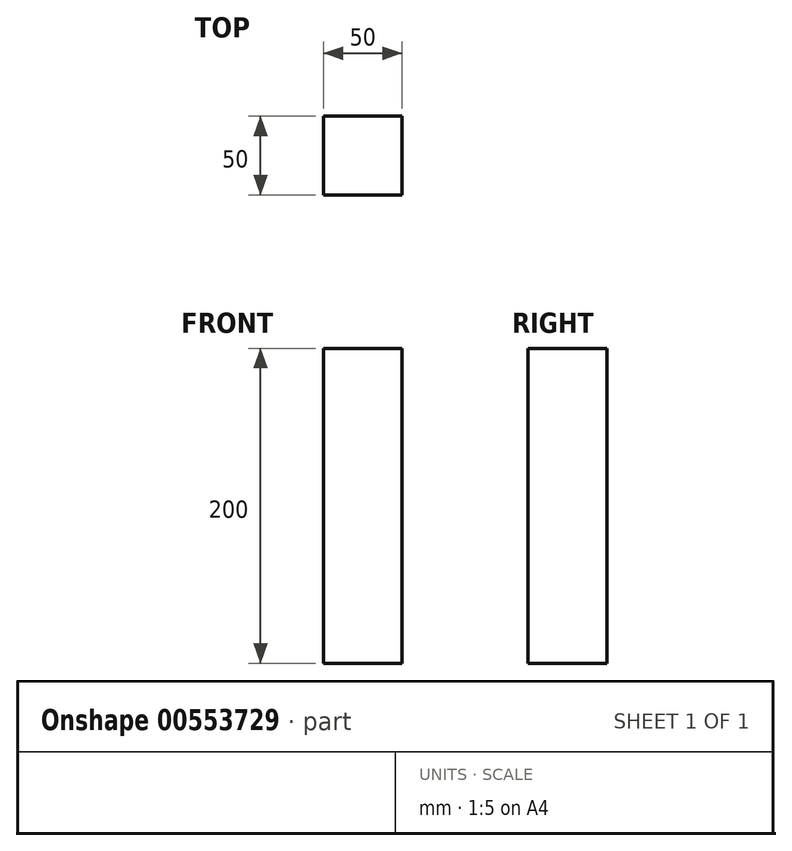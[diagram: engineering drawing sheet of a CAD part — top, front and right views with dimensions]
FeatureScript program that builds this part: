
annotation { "Feature Type Name" : "Feature", "Feature Type Description" : "" }
export const myFeature = defineFeature(function(context is Context, id is Id, definition is map)
    precondition{}
    {
        {
            var Q0;
            Q0=qCreatedBy(makeId("Top.planeOp"), FACE);
            var sketch = newSketch(context, id + "F0", { "sketchPlane" : qUnion([Q0])});
            skLineSegment(sketch, "E0.bottom", {"start": v(25, -25) * mm, "end": v(-25, -25) * mm});
            skLineSegment(sketch, "E0.top", {"start": v(25, 25) * mm, "end": v(-25, 25) * mm});
            skLineSegment(sketch, "E0.left", {"start": v(25, -25) * mm, "end": v(25, 25) * mm});
            skLineSegment(sketch, "E0.right", {"start": v(-25, -25) * mm, "end": v(-25, 25) * mm});
            skPoint(sketch, "E0.middle", {"position": v(0, 0) * mm});
            skSolve(sketch);
        }
        {
            var Q0;
            Q0 = qSketchRegion(id + "F0", true);
            extrude(context, id + "F1", {"entities" : qUnion([Q0]), "depth" : 200 * mm, "offsetDistance" : 25 * mm});
        }
    });
